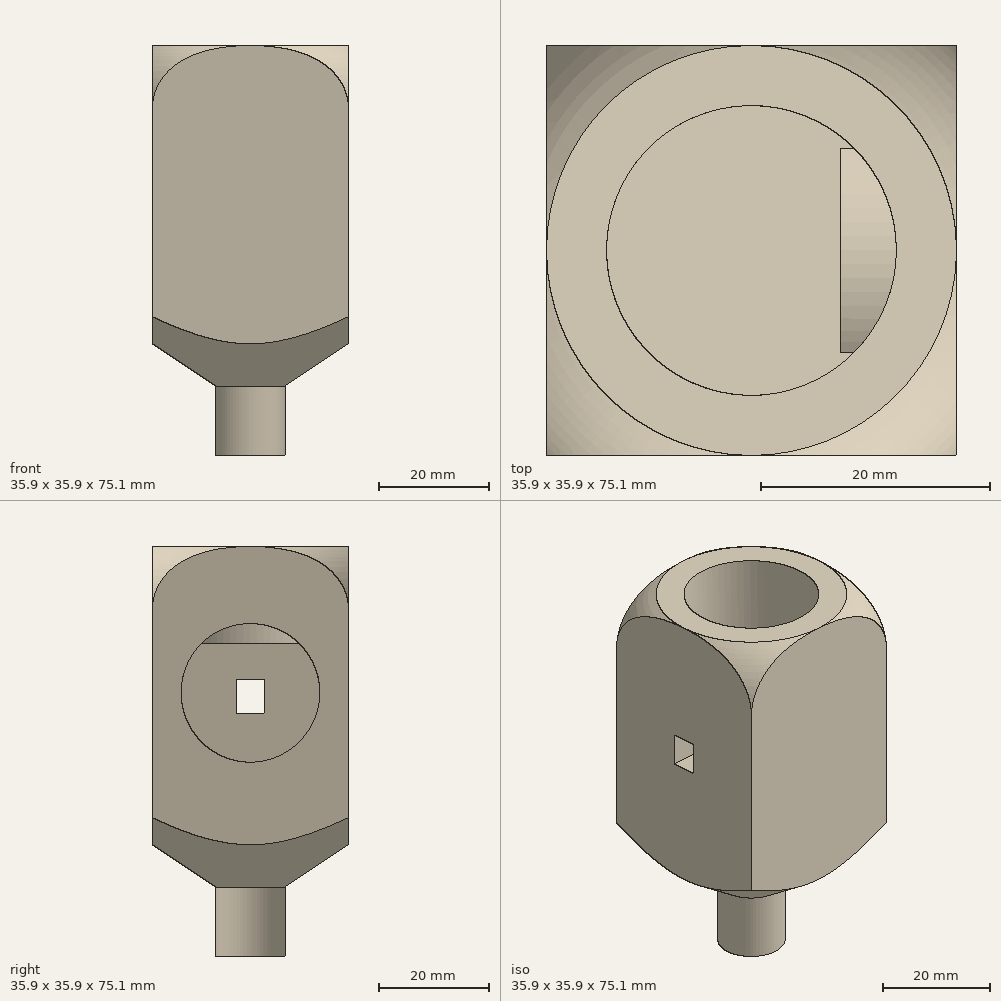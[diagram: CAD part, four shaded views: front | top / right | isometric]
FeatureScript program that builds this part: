
annotation { "Feature Type Name" : "Feature", "Feature Type Description" : "" }
export const myFeature = defineFeature(function(context is Context, id is Id, definition is map)
    precondition{}
    {
        {
            var Q0;
            Q0=qCreatedBy(makeId("Front.planeOp"),FACE);
            var sketch = newSketch(context, id + "F0", { "sketchPlane" : qUnion([Q0])});
            skLineSegment(sketch, "E0", {"start": v(0, 0) * mm, "end": v(6.35, 0) * mm});
            skLineSegment(sketch, "E1", {"start": v(6.35, 0) * mm, "end": v(6.35, 12.7) * mm});
            skLineSegment(sketch, "E2", {"start": v(6.35, 12.7) * mm, "end": v(25.4, 25.4) * mm});
            skLineSegment(sketch, "E3", {"start": v(25.4, 25.4) * mm, "end": v(25.4, 63.5) * mm});
            skLineSegment(sketch, "E4", {"start": v(12.7, 76.2) * mm, "end": v(0, 76.2) * mm});
            skLineSegment(sketch, "E5", {"start": v(0, 76.2) * mm, "end": v(0, 0) * mm});
            skPoint(sketch, "E6.visualSharp", {"position": v(25.4, 76.2) * mm});
            skArc(sketch, "E6.filletArc", {"start": v(25.4, 63.5) * mm, "mid": v(21.68, 72.48) * mm, "end": v(12.7, 76.2) * mm});
            skSolve(sketch);
        }
        {
            var Q0;
            Q0=makeQuery(id+"F0.imprint","IMPRINT",FACE,{"disambiguationData":[TD([[makeQuery(id+"F0.imprint","IMPRINT",EDGE,{"derivedFrom":sQuery(id+"F0.wireOp",EDGE,"E0")}),1.0]])]});
            var Q1;
            Q1=sQuery(id+"F0.wireOp",EDGE,"E5");
            revolve(context, id + "F1", {"entities" : qUnion([Q0]), "axis" : qUnion([Q1]), "revolveType" : RevolveType.FULL});
        }
        {
            var Q0;
            Q0=makeQuery(id+"F1.opRevolve","SWEPT_FACE",FACE,{"disambiguationData":[OSD([sQuery(id+"F0.wireOp",EDGE,"E4")])]});
            var sketch = newSketch(context, id + "F2", { "sketchPlane" : qUnion([Q0])});
            skLineSegment(sketch, "E7.bottom", {"start": v(-25.4, 25.4) * mm, "end": v(25.4, 25.4) * mm});
            skLineSegment(sketch, "E7.top", {"start": v(-25.4, -25.4) * mm, "end": v(25.4, -25.4) * mm});
            skLineSegment(sketch, "E7.left", {"start": v(-25.4, 25.4) * mm, "end": v(-25.4, -25.4) * mm});
            skLineSegment(sketch, "E7.right", {"start": v(25.4, 25.4) * mm, "end": v(25.4, -25.4) * mm});
            skLineSegment(sketch, "E8", {"start": v(-25.4, -25.4) * mm, "end": v(25.4, 25.4) * mm});
            skLineSegment(sketch, "E9", {"start": v(-25.4, 25.4) * mm, "end": v(25.4, -25.4) * mm});
            skLineSegment(sketch, "E10.bottom", {"start": v(-17.96, 17.96) * mm, "end": v(17.96, 17.96) * mm});
            skLineSegment(sketch, "E10.top", {"start": v(-17.96, -17.96) * mm, "end": v(17.96, -17.96) * mm});
            skLineSegment(sketch, "E10.left", {"start": v(-17.96, 17.96) * mm, "end": v(-17.96, -17.96) * mm});
            skLineSegment(sketch, "E10.right", {"start": v(17.96, 17.96) * mm, "end": v(17.96, -17.96) * mm});
            skCircle(sketch, "E11", {"center": v(0, 0) * mm, "radius": 12.7 * mm});
            skSolve(sketch);
        }
        {
            var Q0;
            Q0=makeQuery(id+"F2.imprint","IMPRINT",FACE,{"disambiguationData":[TD([[makeQuery(id+"F2.imprint","IMPRINT",EDGE,{"derivedFrom":sQuery(id+"F2.wireOp",EDGE,"E7.bottom")}),-1.0]])]});
            var Q1;
            {var subQ0=sQuery(id+"F2.wireOp",EDGE,"E7.right");Q1=makeQuery(id+"F2.imprint","IMPRINT",FACE,{"disambiguationData":[TD([[makeQuery(id+"F2.imprint","IMPRINT",EDGE,{"derivedFrom":subQ0}),-1.0]])]});}
            var Q2;
            {var subQ0=sQuery(id+"F2.wireOp",EDGE,"E7.top");Q2=makeQuery(id+"F2.imprint","IMPRINT",FACE,{"disambiguationData":[TD([[makeQuery(id+"F2.imprint","IMPRINT",EDGE,{"derivedFrom":subQ0}),1.0]])]});}
            var Q3;
            {var subQ0=sQuery(id+"F2.wireOp",EDGE,"E7.left");Q3=makeQuery(id+"F2.imprint","IMPRINT",FACE,{"disambiguationData":[TD([[makeQuery(id+"F2.imprint","IMPRINT",EDGE,{"derivedFrom":subQ0}),1.0]])]});}
            var Q4;
            Q4=makeQuery(id+"F1.opRevolve","SWEPT_FACE",FACE,{"disambiguationData":[OSD([sQuery(id+"F0.wireOp",EDGE,"E2")])]});
            extrude(context, id + "F3", {"entities" : qUnion([Q0, Q1, Q2, Q3]), "operationType" : NewBodyOperationType.REMOVE, "endBound" : BoundingType.UP_TO_SURFACE, "oppositeDirection" : true, "endBoundEntityFace" : qUnion([Q4]), "depth" : 25.4 * mm});
        }
        {
            var Q0;
            Q0=qCreatedBy(makeId("Front.planeOp"),FACE);
            var sketch = newSketch(context, id + "F4", { "sketchPlane" : qUnion([Q0])});
            skLineSegment(sketch, "E12.bottom", {"start": v(17.96, 76.2) * mm, "end": v(-18.01, 76.2) * mm});
            skLineSegment(sketch, "E12.top", {"start": v(17.96, 75.06) * mm, "end": v(-18.01, 75.06) * mm});
            skLineSegment(sketch, "E12.left", {"start": v(17.96, 76.2) * mm, "end": v(17.96, 75.06) * mm});
            skLineSegment(sketch, "E12.right", {"start": v(-18.01, 76.2) * mm, "end": v(-18.01, 75.06) * mm});
            skFitSpline(sketch, "E13.0", {"points": [v(17.96, 63.5) * mm, v(17.96, 63.75) * mm, v(17.94, 64.24) * mm, v(17.84, 64.99) * mm, v(17.69, 65.72) * mm, v(17.48, 66.43) * mm, v(17.21, 67.13) * mm, v(16.89, 67.8) * mm, v(16.51, 68.45) * mm, v(16.1, 69.07) * mm, v(15.64, 69.65) * mm, v(15.14, 70.2) * mm, v(14.6, 70.73) * mm, v(13.85, 71.38) * mm, v(13.04, 71.95) * mm, v(12.2, 72.46) * mm, v(11.31, 72.93) * mm, v(10.17, 73.43) * mm, v(8.78, 73.91) * mm, v(7.35, 74.3) * mm, v(5.9, 74.6) * mm, v(4.42, 74.8) * mm, v(2.94, 74.96) * mm, v(1.46, 75.04) * mm, v(-0.53, 75.08) * mm, v(-3, 74.98) * mm, v(-5.43, 74.69) * mm, v(-7.35, 74.3) * mm, v(-8.78, 73.91) * mm, v(-10.2, 73.42) * mm, v(-11.55, 72.82) * mm, v(-12.63, 72.2) * mm, v(-13.46, 71.65) * mm, v(-14.25, 71.05) * mm, v(-15.16, 70.22) * mm, v(-15.96, 69.27) * mm, v(-16.52, 68.44) * mm, v(-17.02, 67.58) * mm, v(-17.4, 66.67) * mm, v(-17.7, 65.71) * mm, v(-17.9, 64.73) * mm, v(-17.96, 64) * mm, v(-17.96, 63.5) * mm]});
            skSolve(sketch);
        }
        {
            var Q0;
            Q0 = qSketchRegion(id + "F4", true);
            extrude(context, id + "F5", {"entities" : qUnion([Q0]), "operationType" : NewBodyOperationType.REMOVE, "endBound" : BoundingType.SYMMETRIC, "oppositeDirection" : true, "depth" : 50.8 * mm});
        }
        {
            var Q0;
            Q0=makeQuery(id+"F5.boolean.opBoolean","COPY",FACE,{"derivedFrom":makeQuery(id+"F5.opExtrude","SWEPT_FACE",FACE,{"disambiguationData":[OSD([sQuery(id+"F4.wireOp",EDGE,"E12.top")])]})});
            var sketch = newSketch(context, id + "F6", { "sketchPlane" : qUnion([Q0])});
            skSolve(sketch);
        }
        {
            var Q0;
            Q0=makeQuery(id+"F3.boolean.opBoolean","COPY",FACE,{"derivedFrom":makeQuery(id+"F3.opExtrude","SWEPT_FACE",FACE,{"disambiguationData":[OSD([sQuery(id+"F2.wireOp",EDGE,"E10.right")])]})});
            var sketch = newSketch(context, id + "F7", { "sketchPlane" : qUnion([Q0])});
            skCircle(sketch, "E14", {"center": v(0, 48.26) * mm, "radius": 12.7 * mm});
            skSolve(sketch);
        }
        {
            var Q0;
            Q0 = qSketchRegion(id + "F7", true);
            extrude(context, id + "F8", {"entities" : qUnion([Q0]), "operationType" : NewBodyOperationType.REMOVE, "oppositeDirection" : true, "depth" : 10.16 * mm});
        }
        {
            var Q0;
            Q0=makeQuery(id+"F3.boolean.opBoolean","COPY",FACE,{"derivedFrom":makeQuery(id+"F3.opExtrude","SWEPT_FACE",FACE,{"disambiguationData":[OSD([sQuery(id+"F2.wireOp",EDGE,"E10.left")])]})});
            var sketch = newSketch(context, id + "F9", { "sketchPlane" : qUnion([Q0])});
            skLineSegment(sketch, "E15.bottom", {"start": v(-2.54, 50.8) * mm, "end": v(2.54, 50.8) * mm});
            skLineSegment(sketch, "E15.top", {"start": v(-2.54, 44.45) * mm, "end": v(2.54, 44.45) * mm});
            skLineSegment(sketch, "E15.left", {"start": v(-2.54, 50.8) * mm, "end": v(-2.54, 44.45) * mm});
            skLineSegment(sketch, "E15.right", {"start": v(2.54, 50.8) * mm, "end": v(2.54, 44.45) * mm});
            skSolve(sketch);
        }
        {
            var Q0;
            Q0 = qSketchRegion(id + "F9", true);
            extrude(context, id + "F10", {"entities" : qUnion([Q0]), "operationType" : NewBodyOperationType.REMOVE, "endBound" : BoundingType.THROUGH_ALL, "oppositeDirection" : true, "depth" : 25.4 * mm});
        }
        {
            var Q0;
            {var subQ0=makeQuery(id+"F5.opExtrude","SWEPT_FACE",FACE,{"disambiguationData":[OSD([sQuery(id+"F4.wireOp",EDGE,"E12.top")])]});var subQ1=makeQuery(id+"F1.opRevolve","SWEPT_FACE",FACE,{"disambiguationData":[OSD([sQuery(id+"F0.wireOp",EDGE,"E6.filletArc")])]});Q0=makeQuery(id+"F6.imprint","IMPRINT",FACE,{"disambiguationData":[TD([[makeQuery(id+"F6.imprint","IMPRINT",EDGE,{"derivedFrom":makeQuery(id+"F5.boolean.opBoolean","INTERSECT",EDGE,{"disambiguationData":[OD(0.0)],"derivedFrom":[subQ1,subQ0]})}),1.0]])]});}
            var sketch = newSketch(context, id + "F11", { "sketchPlane" : qUnion([Q0])});
            skCircle(sketch, "E16", {"center": v(0, 0) * mm, "radius": 12.7 * mm});
            skFitSpline(sketch, "E17.0", {"points": [v(0, 17.96) * mm, v(-5.99, 17.96) * mm, v(-11.97, 17.96) * mm, v(-17.96, 17.96) * mm]});
            skFitSpline(sketch, "E18.0", {"points": [v(17.96, 17.96) * mm, v(11.97, 17.96) * mm, v(5.99, 17.96) * mm, v(0, 17.96) * mm]});
            skFitSpline(sketch, "E19.0", {"points": [v(17.96, 0) * mm, v(17.96, 5.99) * mm, v(17.96, 11.97) * mm, v(17.96, 17.96) * mm]});
            skFitSpline(sketch, "E20.0", {"points": [v(17.96, -17.96) * mm, v(17.96, -11.97) * mm, v(17.96, -5.99) * mm, v(17.96, 0) * mm]});
            skFitSpline(sketch, "E21.0", {"points": [v(17.96, -17.96) * mm, v(11.97, -17.96) * mm, v(5.99, -17.96) * mm, v(0, -17.96) * mm]});
            skFitSpline(sketch, "E22.0", {"points": [v(0, -17.96) * mm, v(-5.99, -17.96) * mm, v(-11.97, -17.96) * mm, v(-17.96, -17.96) * mm]});
            skFitSpline(sketch, "E23.0", {"points": [v(-17.96, -17.96) * mm, v(-17.96, -11.97) * mm, v(-17.96, -5.99) * mm, v(-17.96, 0) * mm]});
            skSolve(sketch);
        }
        {
            var Q0;
            Q0 = qSketchRegion(id + "F11", true);
            extrude(context, id + "F12", {"entities" : qUnion([Q0]), "operationType" : NewBodyOperationType.REMOVE, "oppositeDirection" : true, "depth" : 17.78 * mm});
        }
    });
